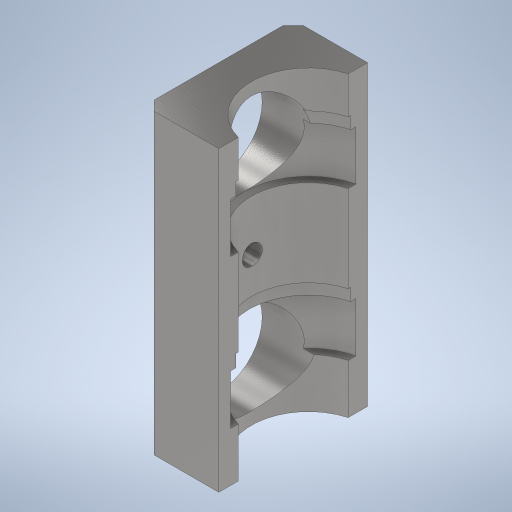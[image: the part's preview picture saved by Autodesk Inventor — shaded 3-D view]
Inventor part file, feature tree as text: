
AUTODESK INVENTOR PART (.ipt)
format: ipt  version: 2024 (Build 280153000, 153)  size: 352,256 bytes
history: native  units: mm
features: sketch x7, extrude x6, plane x2, chamfer x1, hole x1
ambient origin geometry x8: Origin, YZ Plane, XZ Plane, XY Plane, X Axis, Y Axis, Z Axis, Center Point
bodies: Volumenkörper1 (feature_tree)
feature tree (17):
  extrude  "Extrusion1"  Depth=30.0mm
  plane  "Arbeitsebene1"
  extrude  "Extrusion5"  Depth=120.0mm TaperAngle=0.0deg
  plane  "Arbeitsebene2"
  extrude  "Extrusion6"  Depth=52.0mm
  extrude  "Extrusion7"  Depth=100.0mm
  extrude  "Extrusion8"  Depth=20.0mm TaperAngle=0.0deg
  extrude  "Extrusion9"  Depth=5.0mm TaperAngle=0.0deg
  chamfer  "Fasen1"  Distance=5.0mm
  hole  "Bohrung1"  [1 undecoded]
  sketch  "Skizze1"  dims[d3=60.0mm d5=30.0mm]
  sketch  "Skizze4"  dims[d6=23.0mm d7=120.0mm d8=0.0mm]
  sketch  "Skizze5"  dims[d9=40.0mm d20=52.0mm]
  sketch  "Skizze6"  dims[d21=20.0mm d22=0.0mm d23=100.0mm]
  sketch  "Skizze7"  dims[d24=52.0mm d25=20.0mm d26=0.0mm]
  sketch  "Skizze8"  dims[d27=48.0mm d28=5.0mm d29=0.0mm]
  sketch  "Skizze10"  dims[d30=48.0mm d31=5.0mm d32=0.0mm d33=75.0mm d34=35.0mm d35=20.0mm d36=0.0mm d37=4.0mm d38=2.0mm d39=45.0deg d40=8.0mm d41=6.0mm d42=12.0mm d43=2.0mm d44=90.0deg d45=14.0mm d46=0.0mm]
note: 1 required parameter value undecoded (feature->parameter linkage not recoverable at this tier; creation-order binding heuristic only, values carry confidence <= 0.55)
